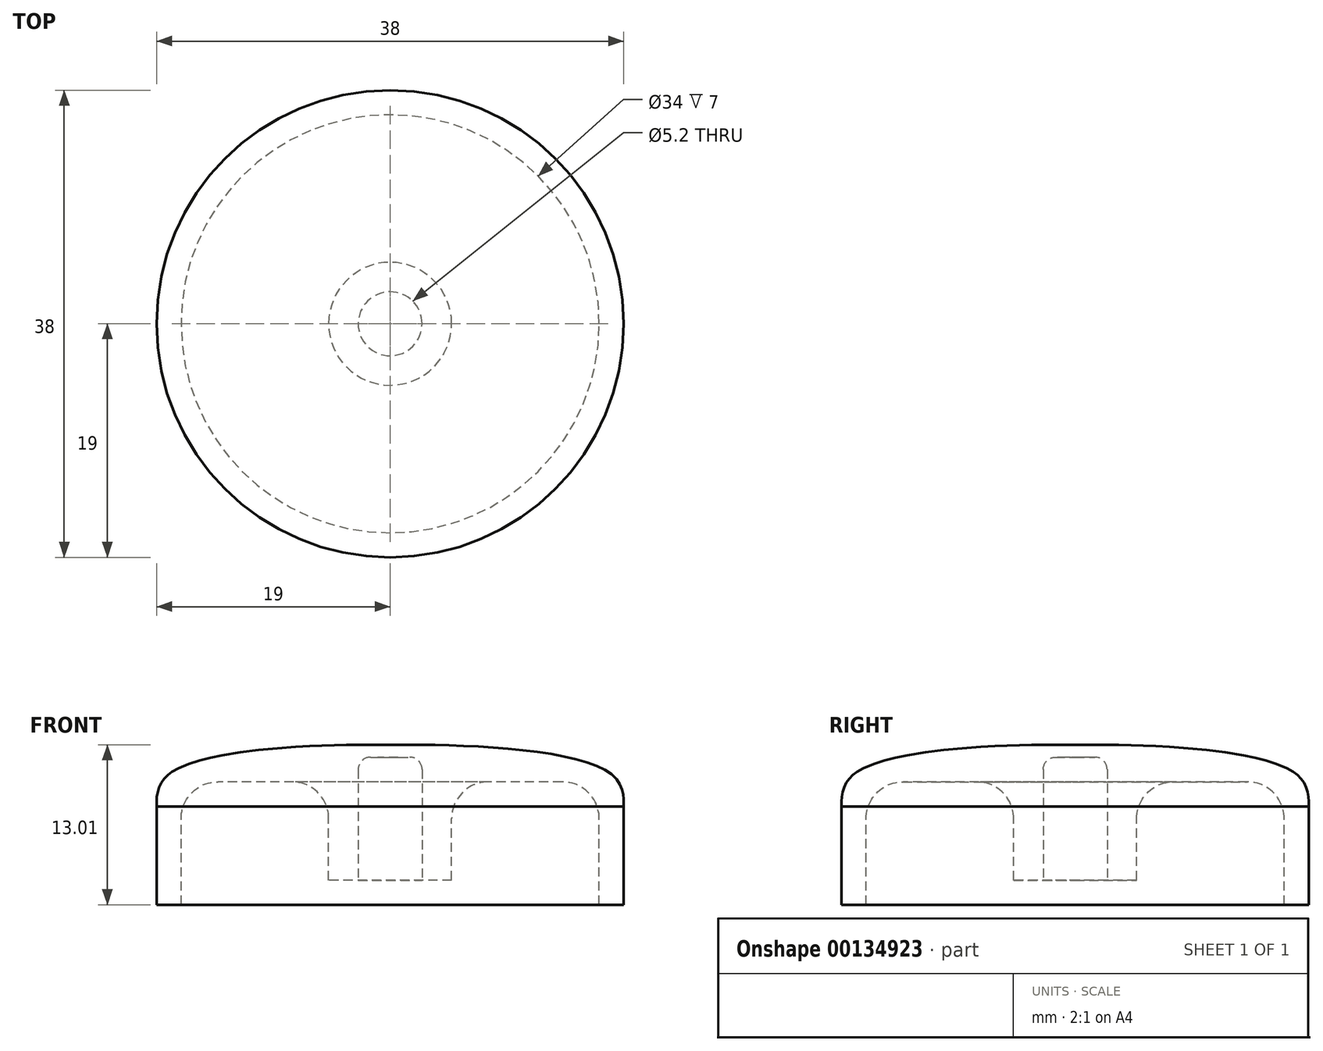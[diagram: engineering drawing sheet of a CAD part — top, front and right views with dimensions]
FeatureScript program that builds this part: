
annotation { "Feature Type Name" : "Feature", "Feature Type Description" : "" }
export const myFeature = defineFeature(function(context is Context, id is Id, definition is map)
    precondition{}
    {
        {
            var Q0;
            Q0=qCreatedBy(makeId("Front.planeOp"),FACE);
            var sketch = newSketch(context, id + "F0", { "sketchPlane" : qUnion([Q0])});
            skLineSegment(sketch, "E0", {"start": v(5, 0) * mm, "end": v(5, 5) * mm});
            skLineSegment(sketch, "E1", {"start": v(8, 8) * mm, "end": v(14, 8) * mm});
            skLineSegment(sketch, "E2", {"start": v(19, -2) * mm, "end": v(19, 6) * mm});
            skLineSegment(sketch, "E3", {"start": v(0, 11) * mm, "end": v(0, 0) * mm});
            skLineSegment(sketch, "E4", {"start": v(0, 0) * mm, "end": v(5, 0) * mm});
            skFitSpline(sketch, "E5", {"points": [v(0, 11) * mm, v(18.05, 8.58) * mm, v(19, 6) * mm], "startDerivative": vector(20.29, 0.3) * mm, "endDerivative": vector(0.16, -5.36) * mm});
            skArc(sketch, "E6.filletArc", {"start": v(8, 8) * mm, "mid": v(5.88, 7.12) * mm, "end": v(5, 5) * mm});
            skArc(sketch, "E7.filletArc", {"start": v(17, 5) * mm, "mid": v(16.12, 7.12) * mm, "end": v(14, 8) * mm});
            skLineSegment(sketch, "E8", {"start": v(17, 5) * mm, "end": v(17, -2) * mm});
            skLineSegment(sketch, "E9", {"start": v(17, -2) * mm, "end": v(19, -2) * mm});
            skSolve(sketch);
        }
        {
            var Q0;
            Q0=qCreatedBy(makeId("Front.planeOp"),FACE);
            var sketch = newSketch(context, id + "F1", { "sketchPlane" : qUnion([Q0])});
            skLineSegment(sketch, "E10", {"start": v(0, 0) * mm, "end": v(2.6, 0) * mm});
            skLineSegment(sketch, "E11", {"start": v(2.6, 0) * mm, "end": v(2.6, 9) * mm});
            skLineSegment(sketch, "E12", {"start": v(1.6, 10) * mm, "end": v(1, 10) * mm});
            skLineSegment(sketch, "E13", {"start": v(0, 9) * mm, "end": v(0, 0) * mm});
            skPoint(sketch, "E14.visualSharp", {"position": v(0, 10) * mm});
            skArc(sketch, "E14.filletArc", {"start": v(1, 10) * mm, "mid": v(0.3, 9.7) * mm, "end": v(0, 9) * mm});
            skPoint(sketch, "E15.visualSharp", {"position": v(2.6, 10) * mm});
            skArc(sketch, "E15.filletArc", {"start": v(2.6, 9) * mm, "mid": v(2.3, 9.7) * mm, "end": v(1.6, 10) * mm});
            skSolve(sketch);
        }
        {
            var Q0;
            Q0 = qSketchRegion(id + "F0", true);
            var Q1;
            Q1=sQuery(id+"F0.wireOp",EDGE,"E3");
            revolve(context, id + "F2", {"entities" : qUnion([Q0]), "axis" : qUnion([Q1]), "revolveType" : RevolveType.FULL});
        }
        {
            var Q0;
            Q0 = qSketchRegion(id + "F1", true);
            var Q1;
            Q1=sQuery(id+"F1.wireOp",EDGE,"E13");
            revolve(context, id + "F3", {"operationType" : NewBodyOperationType.REMOVE, "entities" : qUnion([Q0]), "axis" : qUnion([Q1]), "revolveType" : RevolveType.FULL, "oppositeDirection" : true});
        }
    });
